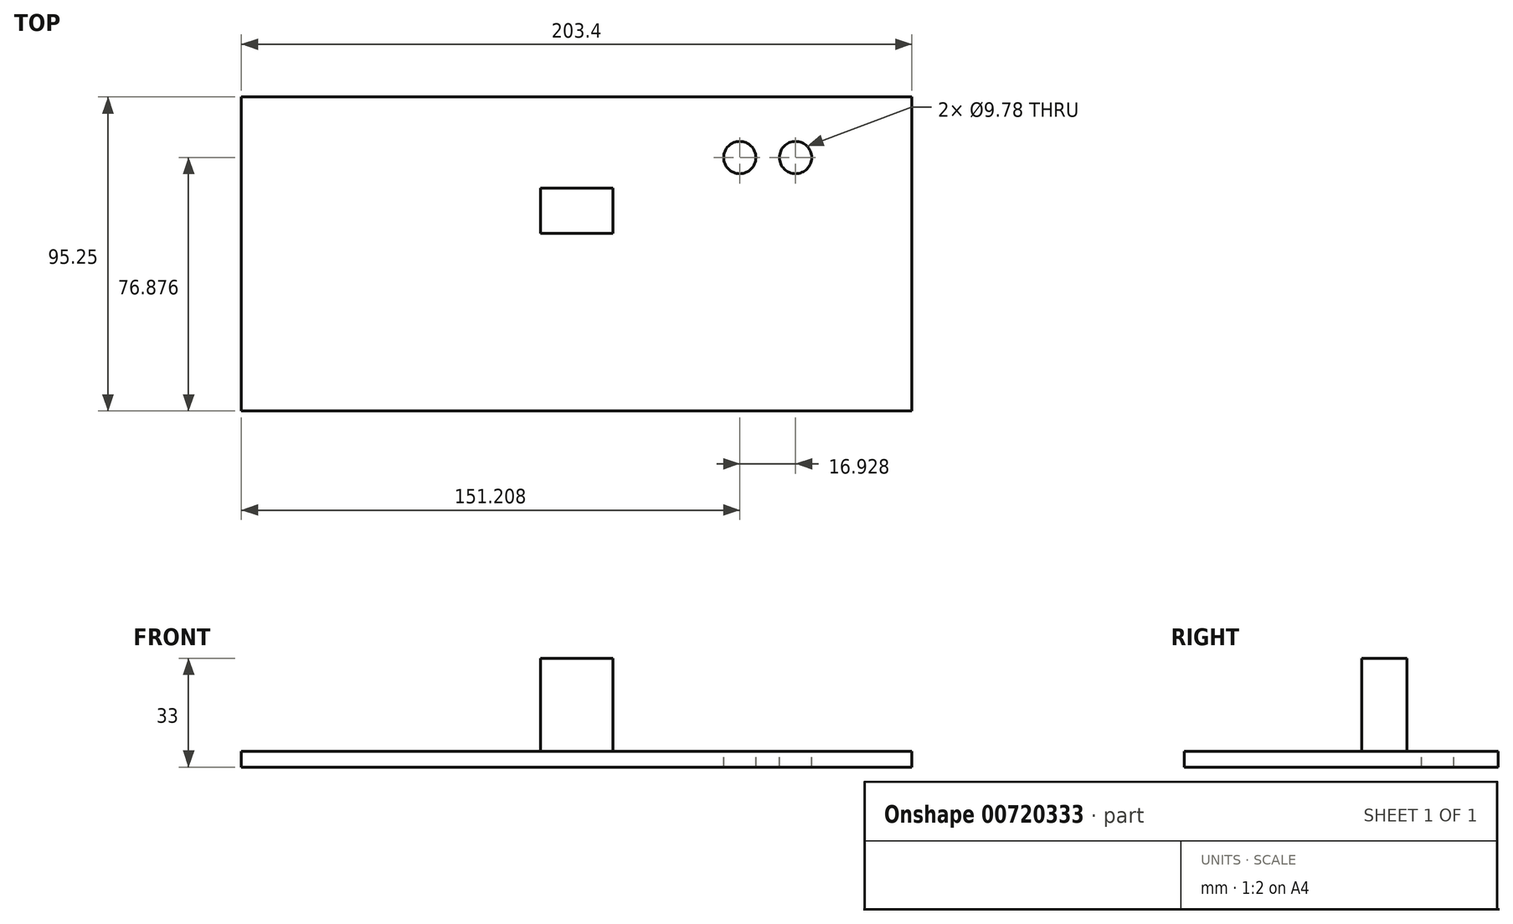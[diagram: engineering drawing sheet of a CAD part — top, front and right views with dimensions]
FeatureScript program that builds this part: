
annotation { "Feature Type Name" : "Feature", "Feature Type Description" : "" }
export const myFeature = defineFeature(function(context is Context, id is Id, definition is map)
    precondition{}
    {
        {
            var Q0;
            Q0=qCreatedBy(makeId("Front.planeOp"),FACE);
            var sketch = newSketch(context, id + "F0", { "sketchPlane" : qUnion([Q0])});
            skLineSegment(sketch, "E0.bottom", {"start": v(101.7, 2.41) * mm, "end": v(-101.7, 2.41) * mm});
            skLineSegment(sketch, "E0.top", {"start": v(101.7, -2.41) * mm, "end": v(-101.7, -2.41) * mm});
            skLineSegment(sketch, "E0.left", {"start": v(101.7, 2.41) * mm, "end": v(101.7, -2.41) * mm});
            skLineSegment(sketch, "E0.right", {"start": v(-101.7, 2.41) * mm, "end": v(-101.7, -2.41) * mm});
            skPoint(sketch, "E0.middle", {"position": v(0, 0) * mm});
            skSolve(sketch);
        }
        {
            var Q0;
            Q0=makeQuery(id+"F0.imprint","IMPRINT",FACE,{"disambiguationData":[TD([[makeQuery(id+"F0.imprint","IMPRINT",EDGE,{"derivedFrom":sQuery(id+"F0.wireOp",EDGE,"E0.bottom")}),1.0]])]});
            extrude(context, id + "F1", {"entities" : qUnion([Q0]), "oppositeDirection" : true, "depth" : 95.25 * mm, "offsetDistance" : 25.4 * mm});
        }
        {
            var Q0;
            Q0=qCreatedBy(makeId("Right.planeOp"),FACE);
            var sketch = newSketch(context, id + "F2", { "sketchPlane" : qUnion([Q0])});
            skLineSegment(sketch, "E1.bottom", {"start": v(53.84, 0) * mm, "end": v(67.56, 0) * mm});
            skLineSegment(sketch, "E1.top", {"start": v(53.84, 30.6) * mm, "end": v(67.56, 30.6) * mm});
            skLineSegment(sketch, "E1.left", {"start": v(53.84, 0) * mm, "end": v(53.84, 30.6) * mm});
            skLineSegment(sketch, "E1.right", {"start": v(67.56, 0) * mm, "end": v(67.56, 30.6) * mm});
            skSolve(sketch);
        }
        {
            var Q0;
            Q0=makeQuery(id+"F2.imprint","IMPRINT",FACE,{"disambiguationData":[TD([[makeQuery(id+"F2.imprint","IMPRINT",EDGE,{"derivedFrom":sQuery(id+"F2.wireOp",EDGE,"E1.bottom")}),1.0]])]});
            extrude(context, id + "F3", {"entities" : qUnion([Q0]), "operationType" : NewBodyOperationType.ADD, "depth" : 11 * mm, "offsetDistance" : 25 * mm});
        }
        {
            var Q0;
            Q0=makeQuery(id+"F3.opExtrude","CAP_FACE",FACE,{"disambiguationData":[OSD([sQuery(id+"F2.wireOp",EDGE,"E1.bottom"),sQuery(id+"F2.wireOp",EDGE,"E1.top"),sQuery(id+"F2.wireOp",EDGE,"E1.left"),sQuery(id+"F2.wireOp",EDGE,"E1.right")])],"isStart":true});
            extrude(context, id + "F4", {"entities" : qUnion([Q0]), "operationType" : NewBodyOperationType.ADD, "depth" : 10.9 * mm, "offsetDistance" : 25 * mm});
        }
        {
            var Q0;
            Q0=makeQuery(id+"F1.opExtrude","SWEPT_FACE",FACE,{"disambiguationData":[OSD([sQuery(id+"F0.wireOp",EDGE,"E0.bottom")])]});
            var sketch = newSketch(context, id + "F5", { "sketchPlane" : qUnion([Q0])});
            skCircle(sketch, "E2", {"center": v(66.44, 76.88) * mm, "radius": 4.9 * mm});
            skCircle(sketch, "E3", {"center": v(49.5, 76.88) * mm, "radius": 4.9 * mm});
            skSolve(sketch);
        }
        {
            var Q0;
            Q0=makeQuery(id+"F5.imprint","IMPRINT",FACE,{"disambiguationData":[TD([[makeQuery(id+"F5.imprint","IMPRINT",EDGE,{"derivedFrom":sQuery(id+"F5.wireOp",EDGE,"E2")}),1.0]])]});
            var Q1;
            Q1=makeQuery(id+"F5.imprint","IMPRINT",FACE,{"disambiguationData":[TD([[makeQuery(id+"F5.imprint","IMPRINT",EDGE,{"derivedFrom":sQuery(id+"F5.wireOp",EDGE,"E3")}),1.0]])]});
            extrude(context, id + "F6", {"entities" : qUnion([Q0, Q1]), "operationType" : NewBodyOperationType.REMOVE, "endBound" : BoundingType.THROUGH_ALL, "oppositeDirection" : true, "depth" : 24.2 * mm, "offsetDistance" : 25 * mm});
        }
    });
